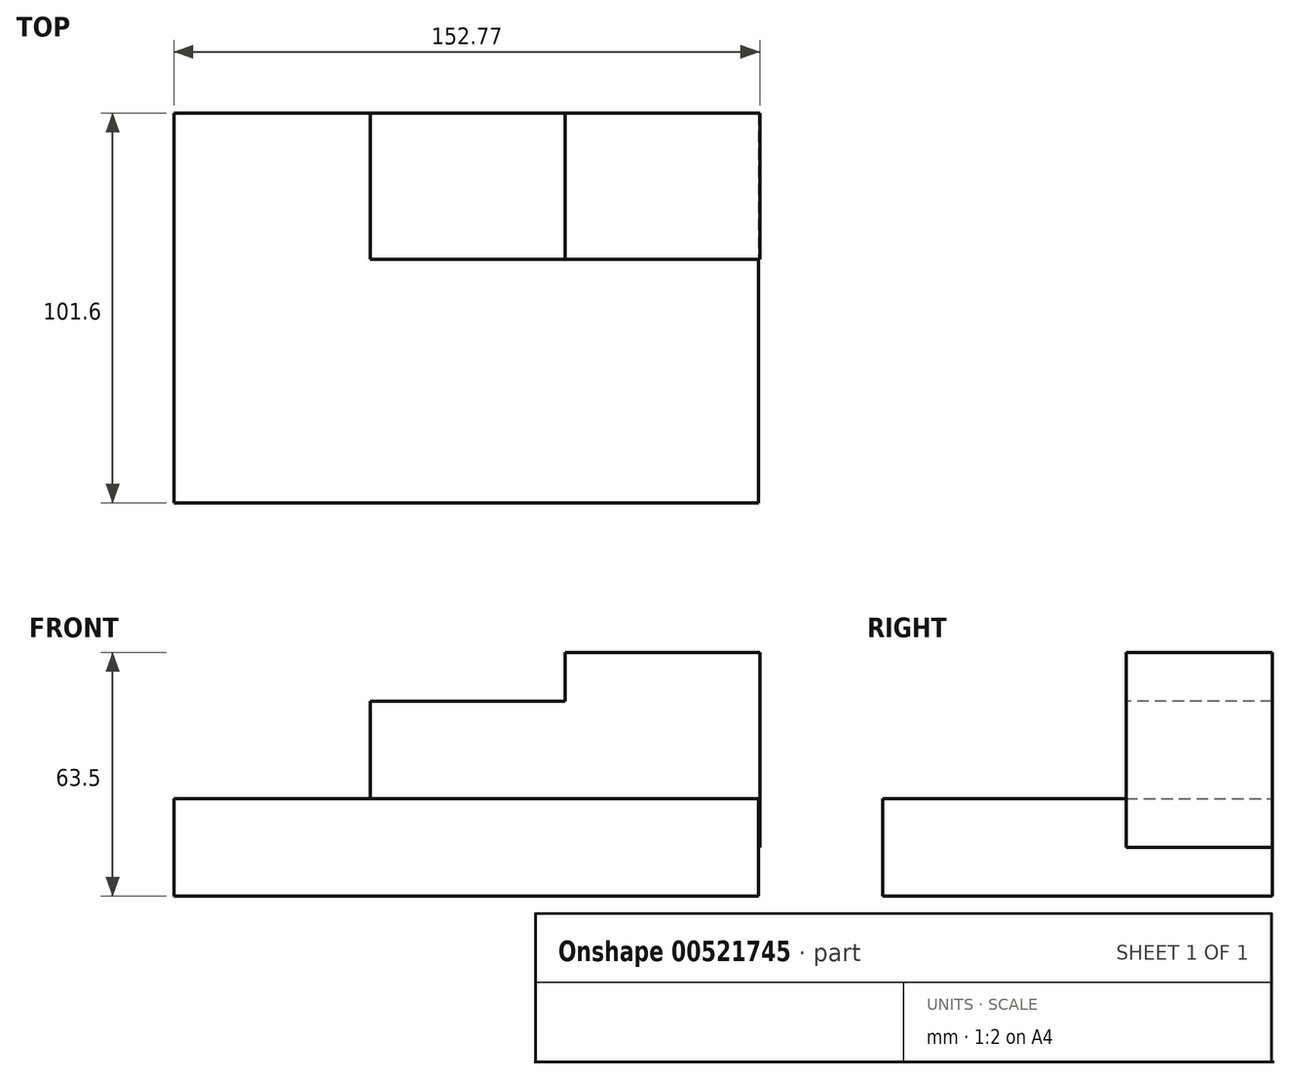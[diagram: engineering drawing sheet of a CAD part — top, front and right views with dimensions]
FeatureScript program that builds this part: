
annotation { "Feature Type Name" : "Feature", "Feature Type Description" : "" }
export const myFeature = defineFeature(function(context is Context, id is Id, definition is map)
    precondition{}
    {
        {
            var Q0;
            Q0=qCreatedBy(makeId("Top.planeOp"),FACE);
            var sketch = newSketch(context, id + "F0", { "sketchPlane" : qUnion([Q0])});
            skLineSegment(sketch, "E0.bottom", {"start": v(-61.93, 48.5) * mm, "end": v(90.47, 48.5) * mm});
            skLineSegment(sketch, "E0.top", {"start": v(-61.93, -53.1) * mm, "end": v(90.47, -53.1) * mm});
            skLineSegment(sketch, "E0.left", {"start": v(-61.93, 48.5) * mm, "end": v(-61.93, -53.1) * mm});
            skLineSegment(sketch, "E0.right", {"start": v(90.47, 48.5) * mm, "end": v(90.47, -53.1) * mm});
            skSolve(sketch);
        }
        {
            var Q0;
            Q0=makeQuery(id+"F0.imprint","IMPRINT",FACE,{"disambiguationData":[TD([[makeQuery(id+"F0.imprint","IMPRINT",EDGE,{"derivedFrom":sQuery(id+"F0.wireOp",EDGE,"E0.bottom")}),-1.0]])]});
            extrude(context, id + "F1", {"entities" : qUnion([Q0]), "depth" : 25.4 * mm, "offsetDistance" : 25.4 * mm, "symmetric" : true});
        }
        {
            var Q0;
            Q0=qCreatedBy(makeId("Top.planeOp"),FACE);
            var sketch = newSketch(context, id + "F2", { "sketchPlane" : qUnion([Q0])});
            skLineSegment(sketch, "E1.bottom", {"start": v(-61.56, 48.5) * mm, "end": v(-10.76, 48.5) * mm});
            skLineSegment(sketch, "E1.top", {"start": v(-61.56, 10.4) * mm, "end": v(-10.76, 10.4) * mm});
            skLineSegment(sketch, "E1.left", {"start": v(-61.56, 48.5) * mm, "end": v(-61.56, 10.4) * mm});
            skLineSegment(sketch, "E1.right", {"start": v(-10.76, 48.5) * mm, "end": v(-10.76, 10.4) * mm});
            skLineSegment(sketch, "E2.bottom", {"start": v(-10.76, 48.5) * mm, "end": v(40.04, 48.5) * mm});
            skLineSegment(sketch, "E2.top", {"start": v(-10.76, 10.4) * mm, "end": v(40.04, 10.4) * mm});
            skLineSegment(sketch, "E2.right", {"start": v(40.04, 48.5) * mm, "end": v(40.04, 10.4) * mm});
            skLineSegment(sketch, "E3.bottom", {"start": v(40.04, 48.5) * mm, "end": v(90.84, 48.5) * mm});
            skLineSegment(sketch, "E3.top", {"start": v(40.04, 10.4) * mm, "end": v(90.84, 10.4) * mm});
            skLineSegment(sketch, "E3.right", {"start": v(90.84, 48.5) * mm, "end": v(90.84, 10.4) * mm});
            skSolve(sketch);
        }
        {
            var Q0;
            Q0=makeQuery(id+"F2.imprint","IMPRINT",FACE,{"disambiguationData":[TD([[makeQuery(id+"F2.imprint","IMPRINT",EDGE,{"derivedFrom":sQuery(id+"F2.wireOp",EDGE,"E3.bottom")}),-1.0]])]});
            extrude(context, id + "F3", {"entities" : qUnion([Q0]), "operationType" : NewBodyOperationType.ADD, "depth" : 50.8 * mm, "offsetDistance" : 25.4 * mm});
        }
        {
            var Q0;
            Q0=makeQuery(id+"F2.imprint","IMPRINT",FACE,{"disambiguationData":[TD([[makeQuery(id+"F2.imprint","IMPRINT",EDGE,{"derivedFrom":sQuery(id+"F2.wireOp",EDGE,"E2.bottom")}),-1.0]])]});
            extrude(context, id + "F4", {"entities" : qUnion([Q0]), "operationType" : NewBodyOperationType.ADD, "depth" : 38.1 * mm, "offsetDistance" : 25.4 * mm});
        }
    });
